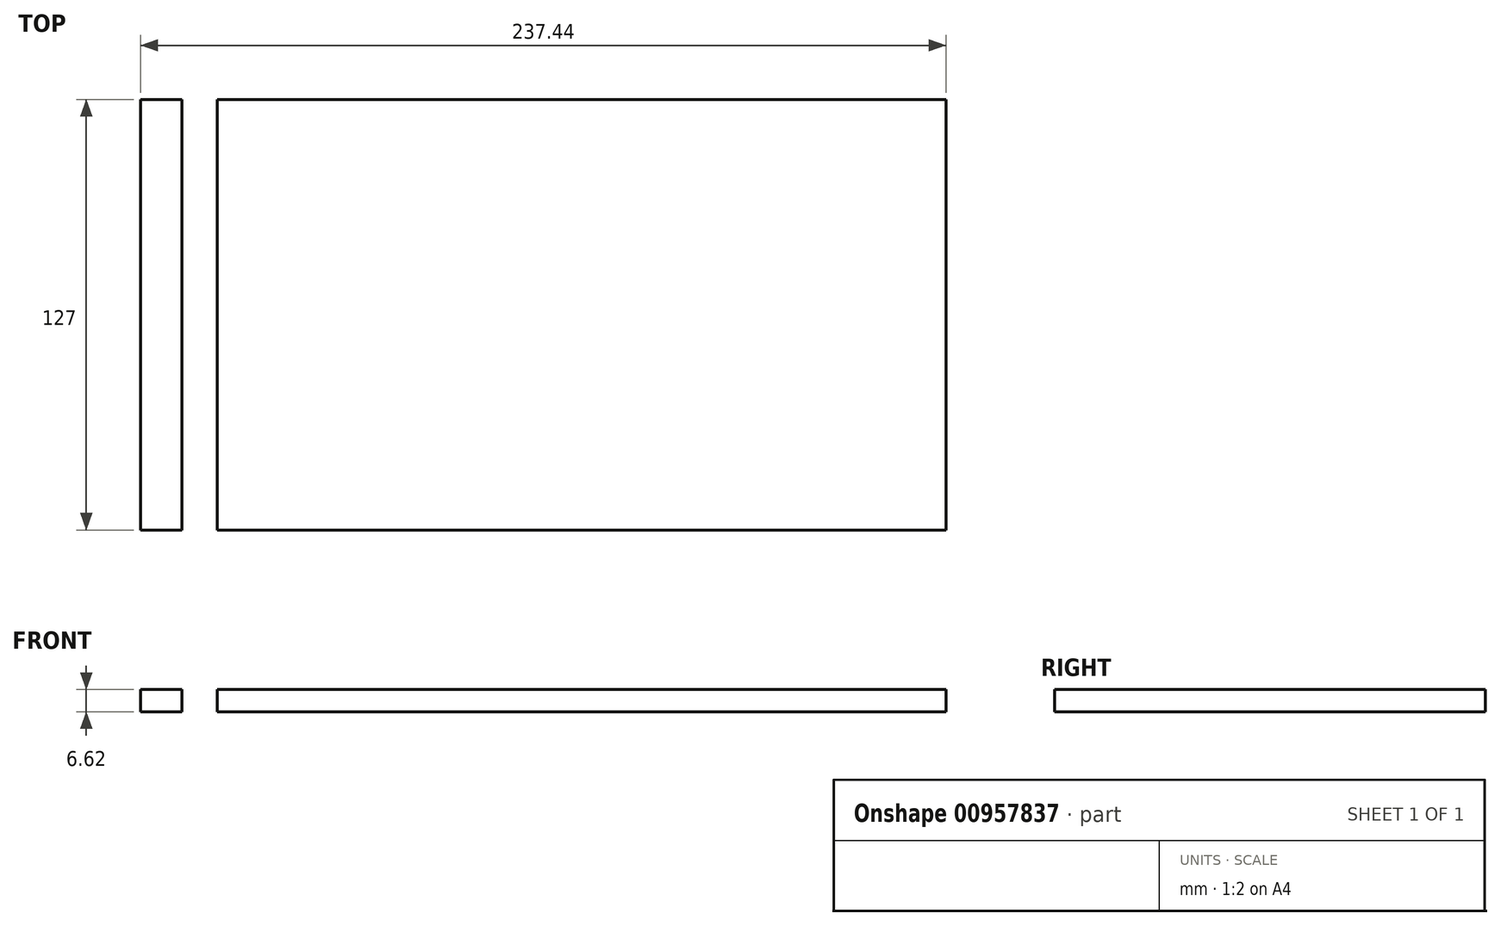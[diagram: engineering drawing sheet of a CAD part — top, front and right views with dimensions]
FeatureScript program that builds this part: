
annotation { "Feature Type Name" : "Feature", "Feature Type Description" : "" }
export const myFeature = defineFeature(function(context is Context, id is Id, definition is map)
    precondition{}
    {
        {
            var Q0;
            Q0=qCreatedBy(makeId("Front.planeOp"),FACE);
            var sketch = newSketch(context, id + "F0", { "sketchPlane" : qUnion([Q0])});
            skLineSegment(sketch, "E0.bottom", {"start": v(-71.8, -17.41) * mm, "end": v(165.63, -17.41) * mm});
            skLineSegment(sketch, "E0.top", {"start": v(-71.8, -24.03) * mm, "end": v(165.63, -24.03) * mm});
            skLineSegment(sketch, "E0.left", {"start": v(-71.8, -17.41) * mm, "end": v(-71.8, -24.03) * mm});
            skLineSegment(sketch, "E0.right", {"start": v(165.63, -17.41) * mm, "end": v(165.63, -24.03) * mm});
            skSolve(sketch);
        }
        {
            var Q0;
            Q0=makeQuery(id+"F0.imprint","IMPRINT",FACE,{"disambiguationData":[TD([[makeQuery(id+"F0.imprint","IMPRINT",EDGE,{"derivedFrom":sQuery(id+"F0.wireOp",EDGE,"E0.bottom")}),-1.0]])]});
            extrude(context, id + "F1", {"entities" : qUnion([Q0]), "depth" : 127 * mm, "offsetDistance" : 25.4 * mm});
        }
        {
            var Q0;
            Q0=makeQuery(id+"F1.opExtrude","SWEPT_FACE",FACE,{"disambiguationData":[OSD([sQuery(id+"F0.wireOp",EDGE,"E0.bottom")])]});
            var sketch = newSketch(context, id + "F2", { "sketchPlane" : qUnion([Q0])});
            skLineSegment(sketch, "E1", {"start": v(-59.7, 0) * mm, "end": v(-59.7, -127) * mm});
            skLineSegment(sketch, "E2", {"start": v(-49.21, 0) * mm, "end": v(-49.21, -127) * mm});
            skSolve(sketch);
        }
        {
            var Q0;
            {var subQ0=sQuery(id+"F2.wireOp",EDGE,"E1");Q0=makeQuery(id+"F2.imprint","IMPRINT",FACE,{"disambiguationData":[TD([[makeQuery(id+"F2.imprint","IMPRINT",EDGE,{"derivedFrom":subQ0}),1.0]])]});}
            extrude(context, id + "F3", {"entities" : qUnion([Q0]), "operationType" : NewBodyOperationType.REMOVE, "oppositeDirection" : true, "depth" : 25.4 * mm, "offsetDistance" : 25.4 * mm});
        }
    });
